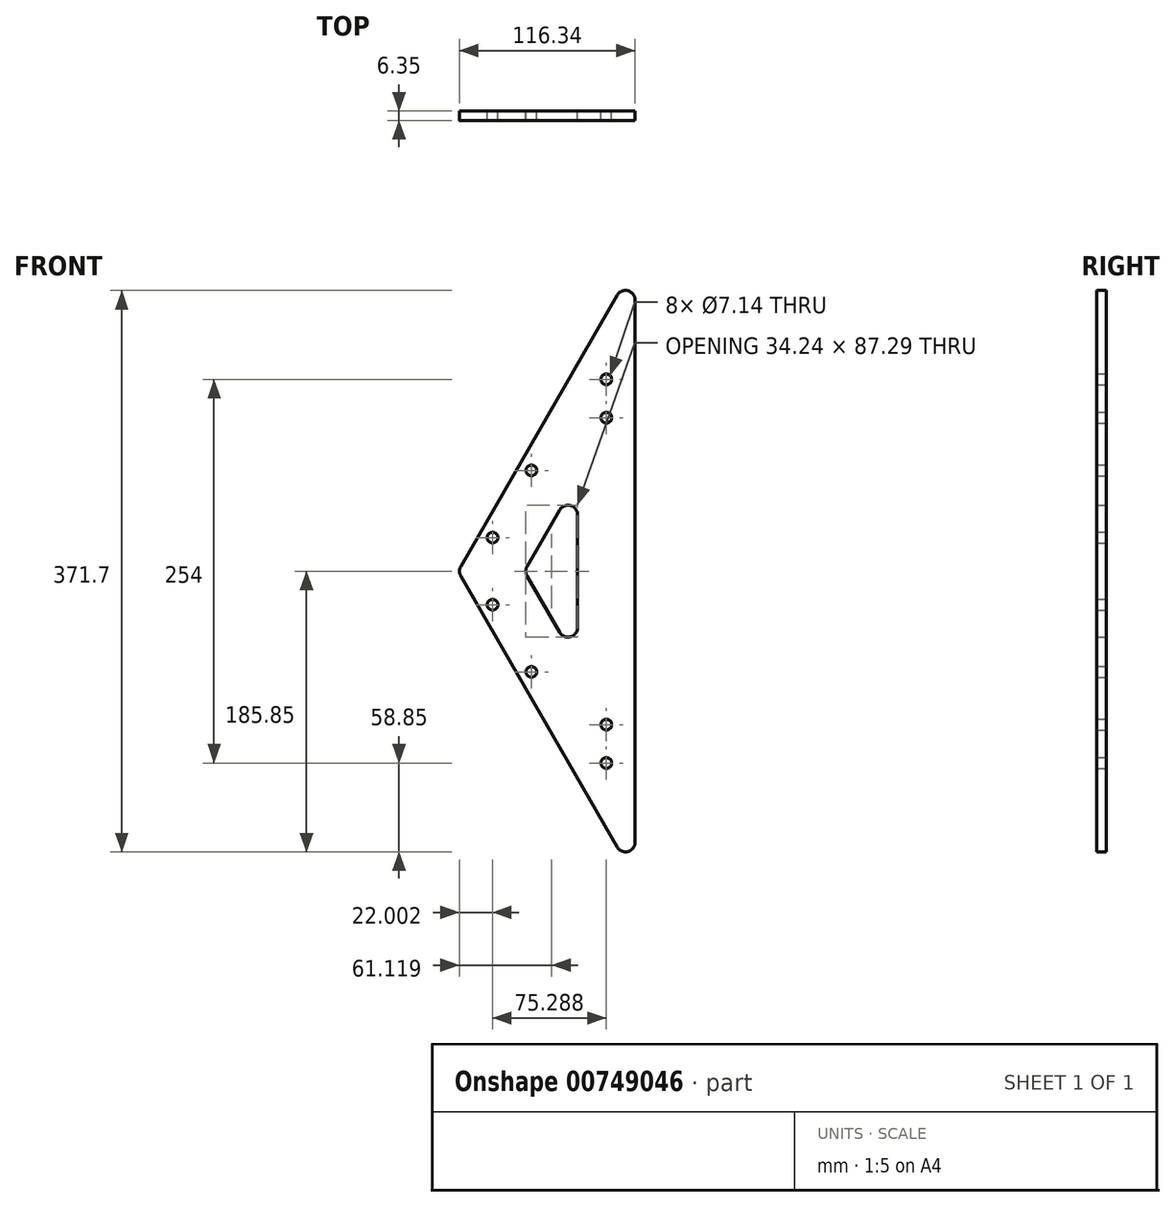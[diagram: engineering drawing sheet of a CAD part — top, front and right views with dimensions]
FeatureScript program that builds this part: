
annotation { "Feature Type Name" : "Feature", "Feature Type Description" : "" }
export const myFeature = defineFeature(function(context is Context, id is Id, definition is map)
    precondition{}
    {
        {
            var Q0;
            Q0=qCreatedBy(makeId("Front.planeOp"),FACE);
            var sketch = newSketch(context, id + "F0", { "sketchPlane" : qUnion([Q0])});
            skLineSegment(sketch, "E0", {"start": v(0, 23.7) * mm, "end": v(0, 382.7) * mm});
            skLineSegment(sketch, "E1", {"start": v(-11.85, 385.88) * mm, "end": v(-115.48, 206.38) * mm});
            skLineSegment(sketch, "E2", {"start": v(-115.48, 200.03) * mm, "end": v(-11.85, 20.52) * mm});
            skLineSegment(sketch, "E3", {"start": v(-38.1, 240.51) * mm, "end": v(-38.1, 165.89) * mm});
            skLineSegment(sketch, "E4", {"start": v(-49.95, 162.71) * mm, "end": v(-71.5, 200.03) * mm});
            skLineSegment(sketch, "E5", {"start": v(-71.5, 206.37) * mm, "end": v(-49.95, 243.69) * mm});
            skPoint(sketch, "E6.visualSharp", {"position": v(0, 406.4) * mm});
            skArc(sketch, "E6.filletArc", {"start": v(0, 382.7) * mm, "mid": v(-4.7, 388.84) * mm, "end": v(-11.85, 385.88) * mm});
            skPoint(sketch, "E7.visualSharp", {"position": v(0, 0) * mm});
            skArc(sketch, "E7.filletArc", {"start": v(-11.85, 20.52) * mm, "mid": v(-4.7, 17.56) * mm, "end": v(0, 23.7) * mm});
            skPoint(sketch, "E8.visualSharp", {"position": v(-117.32, 203.2) * mm});
            skArc(sketch, "E8.filletArc", {"start": v(-115.48, 206.38) * mm, "mid": v(-116.34, 203.2) * mm, "end": v(-115.48, 200.03) * mm});
            skPoint(sketch, "E9.visualSharp", {"position": v(-73.32, 203.2) * mm});
            skArc(sketch, "E9.filletArc", {"start": v(-71.5, 206.37) * mm, "mid": v(-72.34, 203.2) * mm, "end": v(-71.5, 200.03) * mm});
            skPoint(sketch, "E10.visualSharp", {"position": v(-38.1, 264.2) * mm});
            skArc(sketch, "E10.filletArc", {"start": v(-38.1, 240.51) * mm, "mid": v(-42.8, 246.64) * mm, "end": v(-49.95, 243.69) * mm});
            skPoint(sketch, "E11.visualSharp", {"position": v(-38.1, 142.2) * mm});
            skArc(sketch, "E11.filletArc", {"start": v(-49.95, 162.71) * mm, "mid": v(-42.8, 159.76) * mm, "end": v(-38.1, 165.89) * mm});
            skSolve(sketch);
        }
        {
            var Q0;
            Q0 = qSketchRegion(id + "F0", true);
            extrude(context, id + "F1", {"entities" : qUnion([Q0]), "depth" : 6.35 * mm, "offsetDistance" : 25.4 * mm});
        }
        {
            var Q0;
            Q0=makeQuery(id+"F1.opExtrude","CAP_FACE",FACE,{"disambiguationData":[OSD([sQuery(id+"F0.wireOp",EDGE,"E0"),sQuery(id+"F0.wireOp",EDGE,"E1"),sQuery(id+"F0.wireOp",EDGE,"E2"),sQuery(id+"F0.wireOp",EDGE,"E3"),sQuery(id+"F0.wireOp",EDGE,"E4"),sQuery(id+"F0.wireOp",EDGE,"E5"),sQuery(id+"F0.wireOp",EDGE,"E6.filletArc"),sQuery(id+"F0.wireOp",EDGE,"E7.filletArc"),sQuery(id+"F0.wireOp",EDGE,"E8.filletArc"),sQuery(id+"F0.wireOp",EDGE,"E9.filletArc"),sQuery(id+"F0.wireOp",EDGE,"E10.filletArc"),sQuery(id+"F0.wireOp",EDGE,"E11.filletArc")])],"isStart":false});
            var sketch = newSketch(context, id + "F2", { "sketchPlane" : qUnion([Q0])});
            skLineSegment(sketch, "E12", {"start": v(-116.34, 203.2) * mm, "end": v(-72.34, 203.2) * mm, "construction": true});
            skPoint(sketch, "E13.startSnap0", {"position": v(-94.34, 203.2) * mm});
            skLineSegment(sketch, "E14", {"start": v(-94.34, 203.2) * mm, "end": v(-94.34, 243) * mm, "construction": true});
            skPoint(sketch, "E15", {"position": v(-94.34, 225.42) * mm});
            skPoint(sketch, "E16.MirrorP", {"position": v(-94.34, 180.97) * mm});
            skLineSegment(sketch, "E17", {"start": v(-38.1, 203.2) * mm, "end": v(0, 203.2) * mm, "construction": true});
            skLineSegment(sketch, "E18", {"start": v(-19.05, 203.2) * mm, "end": v(-19.05, 373.4) * mm, "construction": true});
            skLineSegment(sketch, "E19", {"start": v(-94.34, 203.2) * mm, "end": v(0, 366.6) * mm, "construction": true});
            skPoint(sketch, "E20", {"position": v(-19.05, 304.8) * mm});
            skPoint(sketch, "E21.MirrorP", {"position": v(-19.05, 101.6) * mm});
            skPoint(sketch, "E22", {"position": v(-19.05, 330.2) * mm});
            skPoint(sketch, "E23.MirrorP", {"position": v(-19.05, 76.2) * mm});
            skLineSegment(sketch, "E24", {"start": v(-94.34, 225.42) * mm, "end": v(-19.05, 355.83) * mm, "construction": true});
            skPoint(sketch, "E25", {"position": v(-68.67, 269.88) * mm});
            skPoint(sketch, "E26.MirrorP", {"position": v(-68.67, 136.53) * mm});
            skSolve(sketch);
        }
        {
            var Q0;
            Q0=sQuery(id+"F2.wireOp",VERTEX,"28efc38b-476b-4d96-b270-5ca697781805");
            var Q1;
            Q1=sQuery(id+"F2.wireOp",VERTEX,"E15");
            var Q2;
            Q2=sQuery(id+"F2.wireOp",VERTEX,"E16.MirrorP");
            var Q3;
            Q3=sQuery(id+"F2.wireOp",VERTEX,"1c58dcd1-1934-4a8b-954f-d9ac7fbd60000.MirrorP");
            var Q4;
            Q4=sQuery(id+"F2.wireOp",VERTEX,"E20");
            var Q5;
            Q5=sQuery(id+"F2.wireOp",VERTEX,"E21.MirrorP");
            var Q6;
            Q6=sQuery(id+"F2.wireOp",VERTEX,"E23.MirrorP");
            var Q7;
            Q7=sQuery(id+"F2.wireOp",VERTEX,"E22");
            var Q8;
            Q8=sQuery(id+"F2.wireOp",VERTEX,"E25");
            var Q9;
            Q9=sQuery(id+"F2.wireOp",VERTEX,"E26.MirrorP");
            var Q10;
            Q10=makeQuery(id+"F1.opExtrude","SWEPT_BODY",BODY,{"disambiguationData":[OSD([sQuery(id+"F0.wireOp",EDGE,"E0"),sQuery(id+"F0.wireOp",EDGE,"E1"),sQuery(id+"F0.wireOp",EDGE,"E2"),sQuery(id+"F0.wireOp",EDGE,"E3"),sQuery(id+"F0.wireOp",EDGE,"E4"),sQuery(id+"F0.wireOp",EDGE,"E5"),sQuery(id+"F0.wireOp",EDGE,"E6.filletArc"),sQuery(id+"F0.wireOp",EDGE,"E7.filletArc"),sQuery(id+"F0.wireOp",EDGE,"E8.filletArc"),sQuery(id+"F0.wireOp",EDGE,"E9.filletArc"),sQuery(id+"F0.wireOp",EDGE,"E10.filletArc"),sQuery(id+"F0.wireOp",EDGE,"E11.filletArc")])]});
            hole(context, id + "F3", {"style" : HoleStyle.SIMPLE, "endStyle" : HoleEndStyle.BLIND, "standardTappedOrClearance" : lookupTablePath({ "fit" : "Normal (ASME)", "standard" : "ANSI", "size" : "1/4", "type" : "Clearance" }), "standardBlindInLast" : lookupTablePath({ "fit" : "Normal", "standard" : "ANSI", "size" : "1/4", "type" : "Clearance" }), "holeDiameter" : 7.14 * mm, "majorDiameter" : 6.35 * mm, "holeDepth" : 304.8 * mm, "isTappedThrough" : true, "tappedDepth" : 301 * mm, "tapClearance" : 3, "locations" : qUnion([Q0, Q1, Q2, Q3, Q4, Q5, Q6, Q7, Q8, Q9]), "scope" : qUnion([Q10])});
        }
    });
